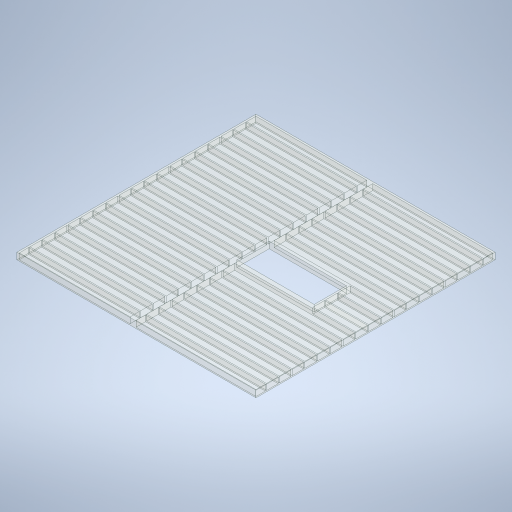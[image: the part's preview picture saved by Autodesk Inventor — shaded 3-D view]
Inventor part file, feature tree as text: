
AUTODESK INVENTOR PART (.ipt)
format: ipt  version: 2024 (Build 280153000, 153)  size: 505,856 bytes
history: native  units: in
note: dims shown in document units (in); Inventor stores cm internally (conversion verified against a paired STEP export)
features: extrude x4, sketch x4
ambient origin geometry x8: Origin, YZ Plane, XZ Plane, XY Plane, X Axis, Y Axis, Z Axis, Center Point
bodies: Solid1 (feature_tree)
feature tree (8):
  extrude  "Extrusion1"  Depth=300.0in
  extrude  "Extrusion2"  Depth=1.5in
  extrude  "Extrusion4"  Depth=140.5in
  extrude  "Extrusion8"  Depth=13.25in
  sketch  "Sketch1"  dims[d1=300.0in d3=300.0in]
  sketch  "Sketch2"  dims[d5=7.5in d6=0.0in d9=1.5in]
  sketch  "Sketch4"  dims[d10=7.5in d11=140.5in]
  sketch  "Sketch8"  dims[d12=1.5in d13=13.25in d14=7.0866in d16=16.0in d17=0.3937in d19=1.0in d21=13.25in d22=0.75in d23=0.0in d32=97.0in d33=129.75in d34=40.5in d35=0.0in d36=0.0in d45=153.75in d46=1.5in d47=7.5in d48=0.0in d38=0.5in d39=0.0344in d40=0.5in d41=0.0344in]
